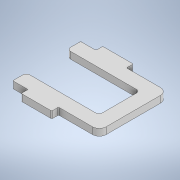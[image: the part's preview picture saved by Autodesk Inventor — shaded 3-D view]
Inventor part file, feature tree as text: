
AUTODESK INVENTOR PART (.ipt)
format: ipt  version: 2021 (Build 250183000, 183)  size: 160,768 bytes
history: native  units: mm
features: extrude x1, fillet x1
ambient origin geometry x8: Origin, YZ Plane, XZ Plane, XY Plane, X Axis, Y Axis, Z Axis, Center Point
bodies: Solid1 (feature_tree)
feature tree (2):
  extrude  "Extrusion1"  Depth=12.0mm
  fillet  "Fillet1"  Radius=2.0mm
